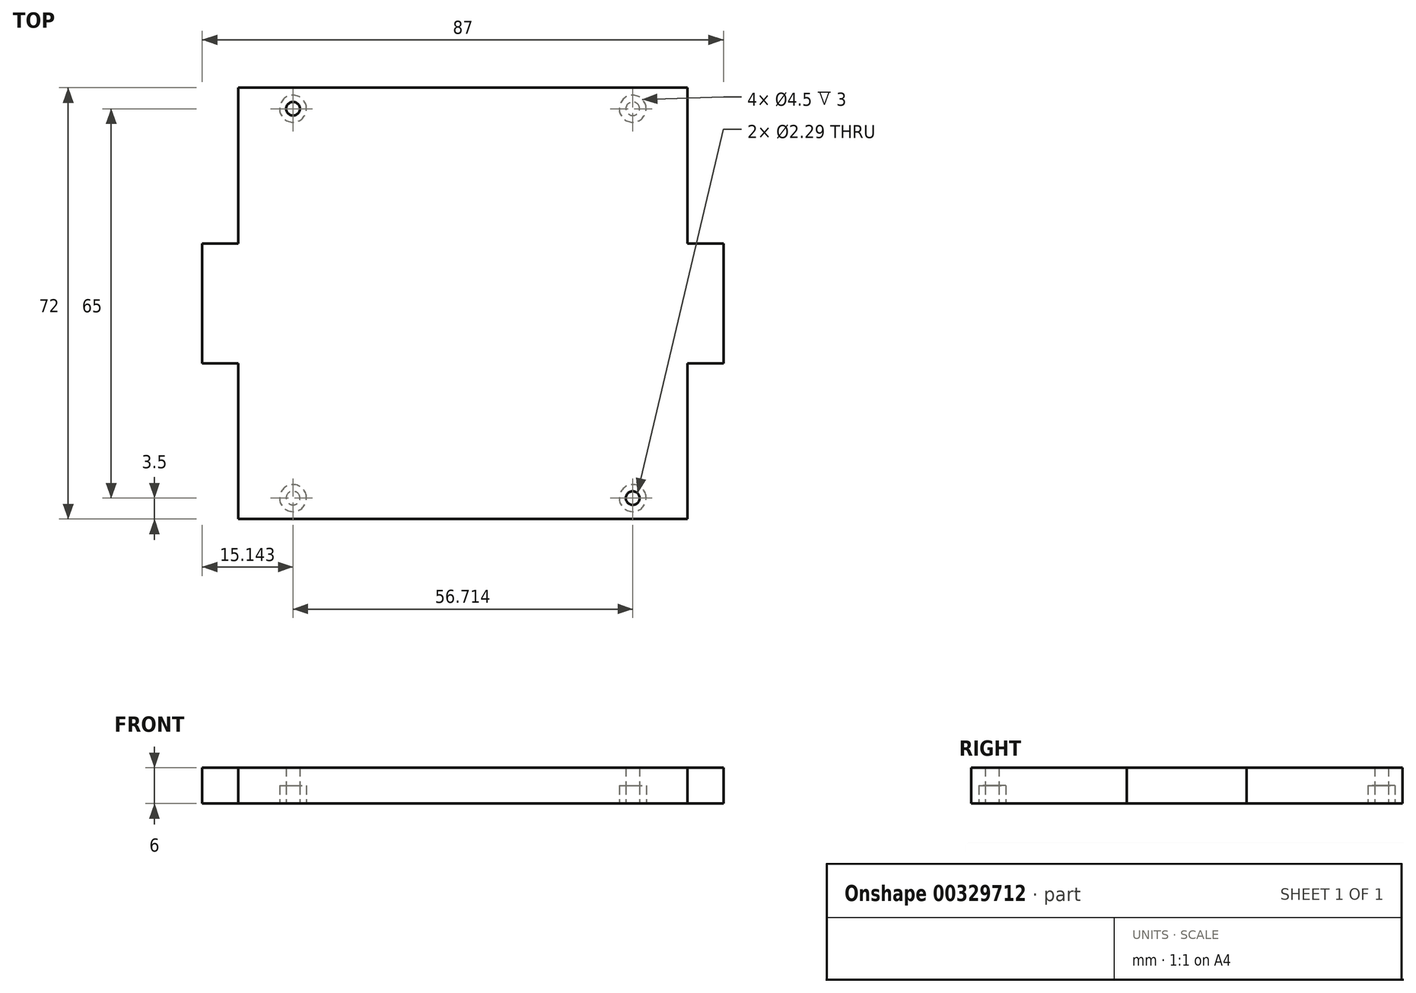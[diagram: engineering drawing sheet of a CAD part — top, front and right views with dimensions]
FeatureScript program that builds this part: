
annotation { "Feature Type Name" : "Feature", "Feature Type Description" : "" }
export const myFeature = defineFeature(function(context is Context, id is Id, definition is map)
    precondition{}
    {
        {
            var Q0;
            Q0=qCreatedBy(makeId("Top.planeOp"),FACE);
            var sketch = newSketch(context, id + "F0", { "sketchPlane" : qUnion([Q0])});
            skLineSegment(sketch, "E0.bottom", {"start": v(37.5, -36) * mm, "end": v(-37.5, -36) * mm});
            skLineSegment(sketch, "E0.top", {"start": v(37.5, 36) * mm, "end": v(-37.5, 36) * mm});
            skLineSegment(sketch, "E0.left", {"start": v(37.5, -36) * mm, "end": v(37.5, 36) * mm});
            skLineSegment(sketch, "E0.right", {"start": v(-37.5, -36) * mm, "end": v(-37.5, 36) * mm});
            skPoint(sketch, "E0.middle", {"position": v(0, 0) * mm});
            skLineSegment(sketch, "E1", {"start": v(-37.5, 10) * mm, "end": v(-43.5, 10) * mm});
            skLineSegment(sketch, "E2", {"start": v(-43.5, 10) * mm, "end": v(-43.5, -10) * mm});
            skLineSegment(sketch, "E3", {"start": v(-43.5, -10) * mm, "end": v(-37.5, -10) * mm});
            skLineSegment(sketch, "E4", {"start": v(37.5, 0) * mm, "end": v(-37.5, 0) * mm, "construction": true});
            skLineSegment(sketch, "E5", {"start": v(0, 36) * mm, "end": v(0, -36) * mm, "construction": true});
            skLineSegment(sketch, "E6.MirrorCS", {"start": v(43.5, -10) * mm, "end": v(37.5, -10) * mm});
            skLineSegment(sketch, "E7.MirrorCS", {"start": v(43.5, 10) * mm, "end": v(43.5, -10) * mm});
            skLineSegment(sketch, "E8.MirrorCS", {"start": v(37.5, 10) * mm, "end": v(43.5, 10) * mm});
            skSolve(sketch);
        }
        {
            var Q0;
            Q0=qSketchRegion(id+"F0",true);
            extrude(context, id + "F1", {"entities" : qUnion([Q0]), "depth" : 6 * mm});
        }
        {
            var Q0;
            Q0=makeQuery(id+"F1.opExtrude","CAP_FACE",FACE,{"disambiguationData":[OSD([sQuery(id+"F0.wireOp",EDGE,"E0.bottom"),sQuery(id+"F0.wireOp",EDGE,"E0.top"),sQuery(id+"F0.wireOp",EDGE,"E0.left"),sQuery(id+"F0.wireOp",EDGE,"E0.right"),sQuery(id+"F0.wireOp",EDGE,"E1"),sQuery(id+"F0.wireOp",EDGE,"E2"),sQuery(id+"F0.wireOp",EDGE,"E3"),sQuery(id+"F0.wireOp",EDGE,"E6.MirrorCS"),sQuery(id+"F0.wireOp",EDGE,"E7.MirrorCS"),sQuery(id+"F0.wireOp",EDGE,"E8.MirrorCS")])],"isStart":true});
            var sketch = newSketch(context, id + "F2", { "sketchPlane" : qUnion([Q0])});
            skLineSegment(sketch, "E9", {"start": v(-43.5, 0) * mm, "end": v(43.5, 0) * mm, "construction": true});
            skLineSegment(sketch, "E10", {"start": v(0, 36) * mm, "end": v(0, -36) * mm, "construction": true});
            skLineSegment(sketch, "E11.bottom", {"start": v(-21, 21) * mm, "end": v(21, 21) * mm, "construction": true});
            skLineSegment(sketch, "E11.top", {"start": v(-21, -21) * mm, "end": v(21, -21) * mm, "construction": true});
            skLineSegment(sketch, "E11.left", {"start": v(-21, 21) * mm, "end": v(-21, -21) * mm, "construction": true});
            skLineSegment(sketch, "E11.right", {"start": v(21, 21) * mm, "end": v(21, -21) * mm, "construction": true});
            skPoint(sketch, "E11.middle", {"position": v(0, 0) * mm});
            skCircle(sketch, "E12", {"center": v(-28.36, -32.5) * mm, "radius": 2.25 * mm});
            skCircle(sketch, "E13.MirrorC", {"center": v(28.36, -32.5) * mm, "radius": 2.25 * mm});
            skCircle(sketch, "E14.MirrorC", {"center": v(-28.36, 32.5) * mm, "radius": 2.25 * mm});
            skCircle(sketch, "E15.MirrorC", {"center": v(28.36, 32.5) * mm, "radius": 2.25 * mm});
            skCircle(sketch, "E16", {"center": v(-28.36, -32.5) * mm, "radius": 1.14 * mm});
            skCircle(sketch, "E17.MirrorC", {"center": v(-28.36, 32.5) * mm, "radius": 1.14 * mm});
            skCircle(sketch, "E18.MirrorC", {"center": v(28.36, 32.5) * mm, "radius": 1.14 * mm});
            skCircle(sketch, "E19.MirrorC", {"center": v(28.36, -32.5) * mm, "radius": 1.14 * mm});
            skSolve(sketch);
        }
        {
            var Q0;
            Q0=qSketchRegion(id+"F2",true);
            extrude(context, id + "F3", {"entities" : qUnion([Q0]), "operationType" : NewBodyOperationType.REMOVE, "oppositeDirection" : true, "depth" : 3 * mm});
        }
        {
            var Q0;
            Q0=makeQuery(id+"F2.imprint","IMPRINT",FACE,{"disambiguationData":[TD([[makeQuery(id+"F2.imprint","IMPRINT",EDGE,{"derivedFrom":sQuery(id+"F2.wireOp",EDGE,"8e4a4935-a642-4271-9785-d91218d17dab0.MirrorC")}),-1.0]])]});
            var Q1;
            Q1=makeQuery(id+"F2.imprint","IMPRINT",FACE,{"disambiguationData":[TD([[makeQuery(id+"F2.imprint","IMPRINT",EDGE,{"derivedFrom":sQuery(id+"F2.wireOp",EDGE,"N4Bc1ARh-4dXR-LxEx-aNHn-Q01SNHtEikhH")}),1.0]])]});
            var Q2;
            Q2=makeQuery(id+"F2.imprint","IMPRINT",FACE,{"disambiguationData":[TD([[makeQuery(id+"F2.imprint","IMPRINT",EDGE,{"derivedFrom":sQuery(id+"F2.wireOp",EDGE,"3bca62c7-e21c-4a76-81b2-2b270dbceb880.MirrorC")}),-1.0]])]});
            var Q3;
            Q3=makeQuery(id+"F2.imprint","IMPRINT",FACE,{"disambiguationData":[TD([[makeQuery(id+"F2.imprint","IMPRINT",EDGE,{"derivedFrom":sQuery(id+"F2.wireOp",EDGE,"ecd9e25a-93bc-4978-b429-abefba4d90550.MirrorC")}),1.0]])]});
            var Q4;
            Q4=makeQuery(id+"F2.imprint","IMPRINT",FACE,{"disambiguationData":[TD([[makeQuery(id+"F2.imprint","IMPRINT",EDGE,{"derivedFrom":sQuery(id+"F2.wireOp",EDGE,"E16")}),1.0]])]});
            var Q5;
            Q5=makeQuery(id+"F2.imprint","IMPRINT",FACE,{"disambiguationData":[TD([[makeQuery(id+"F2.imprint","IMPRINT",EDGE,{"derivedFrom":sQuery(id+"F2.wireOp",EDGE,"E19.MirrorC")}),-1.0]])]});
            var Q6;
            Q6=makeQuery(id+"F2.imprint","IMPRINT",FACE,{"disambiguationData":[TD([[makeQuery(id+"F2.imprint","IMPRINT",EDGE,{"derivedFrom":sQuery(id+"F2.wireOp",EDGE,"E18.MirrorC")}),1.0]])]});
            var Q7;
            Q7=makeQuery(id+"F2.imprint","IMPRINT",FACE,{"disambiguationData":[TD([[makeQuery(id+"F2.imprint","IMPRINT",EDGE,{"derivedFrom":sQuery(id+"F2.wireOp",EDGE,"E17.MirrorC")}),-1.0]])]});
            extrude(context, id + "F4", {"entities" : qUnion([Q0, Q1, Q2, Q3, Q4, Q5, Q6, Q7]), "operationType" : NewBodyOperationType.REMOVE, "endBound" : BoundingType.UP_TO_NEXT, "oppositeDirection" : true, "depth" : 25 * mm});
        }
    });
